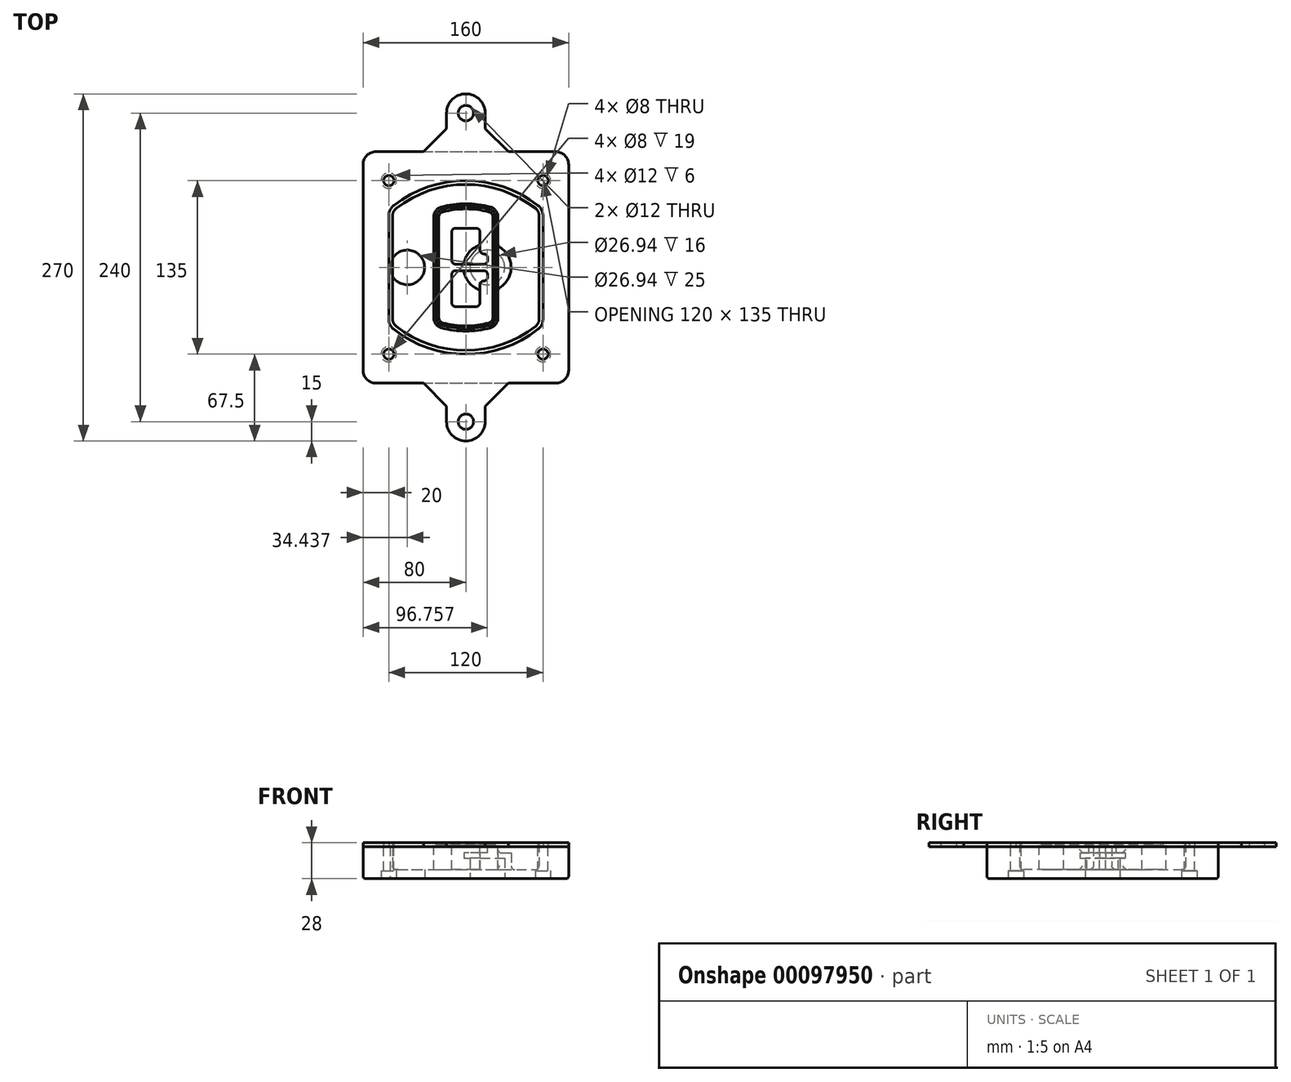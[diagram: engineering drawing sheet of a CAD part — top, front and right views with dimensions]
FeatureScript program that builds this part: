
annotation { "Feature Type Name" : "Feature", "Feature Type Description" : "" }
export const myFeature = defineFeature(function(context is Context, id is Id, definition is map)
    precondition{}
    {
        {
            var Q0;
            Q0=qCreatedBy(makeId("Top.planeOp"),FACE);
            var sketch = newSketch(context, id + "F0", { "sketchPlane" : qUnion([Q0])});
            skPoint(sketch, "E0.rect.middle", {"position": v(0, 0) * mm});
            skLineSegment(sketch, "E1.bottom", {"start": v(-70, -90) * mm, "end": v(70, -90) * mm});
            skLineSegment(sketch, "E1.top", {"start": v(-70, 90) * mm, "end": v(70, 90) * mm});
            skLineSegment(sketch, "E1.left", {"start": v(-80, -80) * mm, "end": v(-80, 80) * mm});
            skLineSegment(sketch, "E1.right", {"start": v(80, -80) * mm, "end": v(80, 80) * mm});
            skLineSegment(sketch, "E2", {"start": v(-80, 90) * mm, "end": v(80, -90) * mm, "construction": true});
            skLineSegment(sketch, "E3", {"start": v(80, 90) * mm, "end": v(-80, -90) * mm, "construction": true});
            skCircle(sketch, "E4", {"center": v(-60, 67.5) * mm, "radius": 4 * mm});
            skCircle(sketch, "E5", {"center": v(60, 67.5) * mm, "radius": 4 * mm});
            skCircle(sketch, "E6", {"center": v(60, -67.5) * mm, "radius": 4 * mm});
            skCircle(sketch, "E7", {"center": v(-60, -67.5) * mm, "radius": 4 * mm});
            skLineSegment(sketch, "E8", {"start": v(-60, 67.5) * mm, "end": v(60, 67.5) * mm, "construction": true});
            skLineSegment(sketch, "E9", {"start": v(60, 67.5) * mm, "end": v(60, -67.5) * mm, "construction": true});
            skLineSegment(sketch, "E10", {"start": v(60, -67.5) * mm, "end": v(-60, -67.5) * mm, "construction": true});
            skLineSegment(sketch, "E11", {"start": v(-60, -67.5) * mm, "end": v(-60, 67.5) * mm, "construction": true});
            skLineSegment(sketch, "E12", {"start": v(-60, 40.3) * mm, "end": v(-60, -40.3) * mm});
            skLineSegment(sketch, "E13", {"start": v(60, 40.3) * mm, "end": v(60, -40.3) * mm});
            skArc(sketch, "E14", {"start": v(56.15, 48.18) * mm, "mid": v(0, 67.5) * mm, "end": v(-56.15, 48.18) * mm});
            skArc(sketch, "E15", {"start": v(-56.15, -48.18) * mm, "mid": v(0, -67.5) * mm, "end": v(56.15, -48.18) * mm});
            skLineSegment(sketch, "E16", {"start": v(-60, 0) * mm, "end": v(60, 0) * mm, "construction": true});
            skPoint(sketch, "E17.visualSharp", {"position": v(-60, -45) * mm});
            skArc(sketch, "E17.filletArc", {"start": v(-60, -40.3) * mm, "mid": v(-58.99, -44.68) * mm, "end": v(-56.15, -48.18) * mm});
            skPoint(sketch, "E18.visualSharp", {"position": v(-60, 45) * mm});
            skArc(sketch, "E18.filletArc", {"start": v(-56.15, 48.18) * mm, "mid": v(-58.99, 44.68) * mm, "end": v(-60, 40.3) * mm});
            skPoint(sketch, "E19.visualSharp", {"position": v(60, 45) * mm});
            skArc(sketch, "E19.filletArc", {"start": v(60, 40.3) * mm, "mid": v(58.99, 44.68) * mm, "end": v(56.15, 48.18) * mm});
            skPoint(sketch, "E20.visualSharp", {"position": v(60, -45) * mm});
            skArc(sketch, "E20.filletArc", {"start": v(56.15, -48.18) * mm, "mid": v(58.99, -44.68) * mm, "end": v(60, -40.3) * mm});
            skPoint(sketch, "E21.visualSharp", {"position": v(-80, 90) * mm});
            skArc(sketch, "E21.filletArc", {"start": v(-70, 90) * mm, "mid": v(-77.07, 87.07) * mm, "end": v(-80, 80) * mm});
            skPoint(sketch, "E22.visualSharp", {"position": v(80, 90) * mm});
            skArc(sketch, "E22.filletArc", {"start": v(80, 80) * mm, "mid": v(77.07, 87.07) * mm, "end": v(70, 90) * mm});
            skPoint(sketch, "E23.visualSharp", {"position": v(80, -90) * mm});
            skArc(sketch, "E23.filletArc", {"start": v(70, -90) * mm, "mid": v(77.07, -87.07) * mm, "end": v(80, -80) * mm});
            skPoint(sketch, "E24.visualSharp", {"position": v(-80, -90) * mm});
            skArc(sketch, "E24.filletArc", {"start": v(-80, -80) * mm, "mid": v(-77.07, -87.07) * mm, "end": v(-70, -90) * mm});
            skArc(sketch, "E25.0", {"start": v(57, 40.3) * mm, "mid": v(56.3, 43.36) * mm, "end": v(54.3, 45.81) * mm});
            skLineSegment(sketch, "E25.1", {"start": v(57, 40.3) * mm, "end": v(57, -40.3) * mm});
            skArc(sketch, "E25.2", {"start": v(54.3, -45.81) * mm, "mid": v(56.3, -43.36) * mm, "end": v(57, -40.3) * mm});
            skArc(sketch, "E25.3", {"start": v(-54.3, -45.81) * mm, "mid": v(0, -64.5) * mm, "end": v(54.3, -45.81) * mm});
            skArc(sketch, "E25.4", {"start": v(-57, -40.3) * mm, "mid": v(-56.3, -43.36) * mm, "end": v(-54.3, -45.81) * mm});
            skArc(sketch, "E25.5", {"start": v(54.3, 45.81) * mm, "mid": v(0, 64.5) * mm, "end": v(-54.3, 45.81) * mm});
            skLineSegment(sketch, "E25.6", {"start": v(-57, 40.3) * mm, "end": v(-57, -40.3) * mm});
            skArc(sketch, "E25.7", {"start": v(-54.3, 45.81) * mm, "mid": v(-56.3, 43.36) * mm, "end": v(-57, 40.3) * mm});
            skArc(sketch, "E26.0", {"start": v(-58.62, 51.33) * mm, "mid": v(-62.58, 46.43) * mm, "end": v(-64, 40.3) * mm});
            skArc(sketch, "E26.1", {"start": v(58.62, 51.33) * mm, "mid": v(0, 71.5) * mm, "end": v(-58.62, 51.33) * mm});
            skArc(sketch, "E26.2", {"start": v(64, 40.3) * mm, "mid": v(62.58, 46.43) * mm, "end": v(58.62, 51.33) * mm});
            skLineSegment(sketch, "E26.3", {"start": v(64, 40.3) * mm, "end": v(64, -40.3) * mm});
            skArc(sketch, "E26.4", {"start": v(58.62, -51.33) * mm, "mid": v(62.58, -46.43) * mm, "end": v(64, -40.3) * mm});
            skLineSegment(sketch, "E26.5", {"start": v(-64, 40.3) * mm, "end": v(-64, -40.3) * mm});
            skArc(sketch, "E26.6", {"start": v(-58.62, -51.33) * mm, "mid": v(0, -71.5) * mm, "end": v(58.62, -51.33) * mm});
            skArc(sketch, "E26.7", {"start": v(-64, -40.3) * mm, "mid": v(-62.58, -46.43) * mm, "end": v(-58.62, -51.33) * mm});
            skSolve(sketch);
        }
        {
            var Q0;
            Q0=makeQuery(id+"F0.imprint","IMPRINT",FACE,{"disambiguationData":[TD([[makeQuery(id+"F0.imprint","IMPRINT",EDGE,{"derivedFrom":sQuery(id+"F0.wireOp",EDGE,"E1.bottom")}),1.0]])]});
            var Q1;
            Q1=makeQuery(id+"F0.imprint","IMPRINT",FACE,{"disambiguationData":[TD([[makeQuery(id+"F0.imprint","IMPRINT",EDGE,{"derivedFrom":sQuery(id+"F0.wireOp",EDGE,"E12")}),1.0]])]});
            var Q2;
            Q2=makeQuery(id+"F0.imprint","IMPRINT",FACE,{"disambiguationData":[TD([[makeQuery(id+"F0.imprint","IMPRINT",EDGE,{"derivedFrom":sQuery(id+"F0.wireOp",EDGE,"E25.0")}),1.0]])]});
            var Q3;
            Q3=makeQuery(id+"F0.imprint","IMPRINT",FACE,{"disambiguationData":[TD([[makeQuery(id+"F0.imprint","IMPRINT",EDGE,{"derivedFrom":sQuery(id+"F0.wireOp",EDGE,"E12")}),-1.0]])]});
            extrude(context, id + "F1", {"entities" : qUnion([Q0, Q1, Q2, Q3]), "oppositeDirection" : true, "depth" : 25 * mm});
        }
        {
            var Q0;
            Q0=makeQuery(id+"F0.imprint","IMPRINT",FACE,{"disambiguationData":[TD([[makeQuery(id+"F0.imprint","IMPRINT",EDGE,{"derivedFrom":sQuery(id+"F0.wireOp",EDGE,"E12")}),1.0]])]});
            extrude(context, id + "F2", {"entities" : qUnion([Q0]), "operationType" : NewBodyOperationType.ADD, "depth" : 3 * mm});
        }
        {
            var Q0;
            Q0=makeQuery(id+"F0.imprint","IMPRINT",FACE,{"disambiguationData":[TD([[makeQuery(id+"F0.imprint","IMPRINT",EDGE,{"derivedFrom":sQuery(id+"F0.wireOp",EDGE,"E25.0")}),1.0]])]});
            extrude(context, id + "F3", {"entities" : qUnion([Q0]), "operationType" : NewBodyOperationType.REMOVE, "oppositeDirection" : true, "depth" : 18 * mm});
        }
        {
            var Q0;
            Q0=makeQuery(id+"F2.opExtrude","CAP_FACE",FACE,{"disambiguationData":[OSD([sQuery(id+"F0.wireOp",EDGE,"E12"),sQuery(id+"F0.wireOp",EDGE,"E13"),sQuery(id+"F0.wireOp",EDGE,"E14"),sQuery(id+"F0.wireOp",EDGE,"E15"),sQuery(id+"F0.wireOp",EDGE,"E17.filletArc"),sQuery(id+"F0.wireOp",EDGE,"E18.filletArc"),sQuery(id+"F0.wireOp",EDGE,"E19.filletArc"),sQuery(id+"F0.wireOp",EDGE,"E20.filletArc"),sQuery(id+"F0.wireOp",EDGE,"E25.0"),sQuery(id+"F0.wireOp",EDGE,"E25.1"),sQuery(id+"F0.wireOp",EDGE,"E25.2"),sQuery(id+"F0.wireOp",EDGE,"E25.3"),sQuery(id+"F0.wireOp",EDGE,"E25.4"),sQuery(id+"F0.wireOp",EDGE,"E25.5"),sQuery(id+"F0.wireOp",EDGE,"E25.6"),sQuery(id+"F0.wireOp",EDGE,"E25.7")])],"isStart":false});
            var sketch = newSketch(context, id + "F4", { "sketchPlane" : qUnion([Q0])});
            skArc(sketch, "E27.0", {"start": v(-19.08, -46.97) * mm, "mid": v(0, -49.5) * mm, "end": v(19.08, -46.97) * mm});
            skArc(sketch, "E28.0", {"start": v(19.08, 46.97) * mm, "mid": v(0, 49.5) * mm, "end": v(-19.08, 46.97) * mm});
            skLineSegment(sketch, "E29", {"start": v(-25, 39.25) * mm, "end": v(-25, -39.25) * mm});
            skLineSegment(sketch, "E30", {"start": v(25, 39.25) * mm, "end": v(25, -39.25) * mm});
            skLineSegment(sketch, "E31", {"start": v(-25, 45.1) * mm, "end": v(25, 45.1) * mm, "construction": true});
            skLineSegment(sketch, "E32", {"start": v(-25, -45.1) * mm, "end": v(25, -45.1) * mm, "construction": true});
            skPoint(sketch, "E33.visualSharp", {"position": v(-25, 45.1) * mm});
            skArc(sketch, "E33.filletArc", {"start": v(-19.08, 46.97) * mm, "mid": v(-23.35, 44.11) * mm, "end": v(-25, 39.25) * mm});
            skPoint(sketch, "E34.visualSharp", {"position": v(25, 45.1) * mm});
            skArc(sketch, "E34.filletArc", {"start": v(25, 39.25) * mm, "mid": v(23.35, 44.11) * mm, "end": v(19.08, 46.97) * mm});
            skPoint(sketch, "E35.visualSharp", {"position": v(25, -45.1) * mm});
            skArc(sketch, "E35.filletArc", {"start": v(19.08, -46.97) * mm, "mid": v(23.35, -44.11) * mm, "end": v(25, -39.25) * mm});
            skPoint(sketch, "E36.visualSharp", {"position": v(-25, -45.1) * mm});
            skArc(sketch, "E36.filletArc", {"start": v(-25, -39.25) * mm, "mid": v(-23.35, -44.11) * mm, "end": v(-19.08, -46.97) * mm});
            skArc(sketch, "E37.0", {"start": v(54.3, 45.81) * mm, "mid": v(0, 64.5) * mm, "end": v(-54.3, 45.81) * mm});
            skArc(sketch, "E37.1", {"start": v(-54.3, 45.81) * mm, "mid": v(-56.3, 43.36) * mm, "end": v(-57, 40.3) * mm});
            skLineSegment(sketch, "E37.2", {"start": v(-57, 40.3) * mm, "end": v(-57, -40.3) * mm});
            skArc(sketch, "E37.3", {"start": v(-57, -40.3) * mm, "mid": v(-56.3, -43.36) * mm, "end": v(-54.3, -45.81) * mm});
            skArc(sketch, "E37.4", {"start": v(-54.3, -45.81) * mm, "mid": v(0, -64.5) * mm, "end": v(54.3, -45.81) * mm});
            skArc(sketch, "E37.5", {"start": v(54.3, -45.81) * mm, "mid": v(56.3, -43.36) * mm, "end": v(57, -40.3) * mm});
            skLineSegment(sketch, "E37.6", {"start": v(57, 40.3) * mm, "end": v(57, -40.3) * mm});
            skArc(sketch, "E37.7", {"start": v(57, 40.3) * mm, "mid": v(56.3, 43.36) * mm, "end": v(54.3, 45.81) * mm});
            skLineSegment(sketch, "E38.0", {"start": v(23, 39.25) * mm, "end": v(23, -39.25) * mm});
            skArc(sketch, "E38.1", {"start": v(18.56, -45.04) * mm, "mid": v(21.76, -42.9) * mm, "end": v(23, -39.25) * mm});
            skArc(sketch, "E38.2", {"start": v(-18.56, -45.04) * mm, "mid": v(0, -47.5) * mm, "end": v(18.56, -45.04) * mm});
            skArc(sketch, "E38.3", {"start": v(-23, -39.25) * mm, "mid": v(-21.76, -42.9) * mm, "end": v(-18.56, -45.04) * mm});
            skLineSegment(sketch, "E38.4", {"start": v(-23, 39.25) * mm, "end": v(-23, -39.25) * mm});
            skArc(sketch, "E38.5", {"start": v(23, 39.25) * mm, "mid": v(21.76, 42.9) * mm, "end": v(18.56, 45.04) * mm});
            skArc(sketch, "E38.6", {"start": v(-18.56, 45.04) * mm, "mid": v(-21.76, 42.9) * mm, "end": v(-23, 39.25) * mm});
            skArc(sketch, "E38.7", {"start": v(18.56, 45.04) * mm, "mid": v(0, 47.5) * mm, "end": v(-18.56, 45.04) * mm});
            skArc(sketch, "E39.0", {"start": v(21, 39.25) * mm, "mid": v(20.18, 41.68) * mm, "end": v(18.04, 43.1) * mm});
            skLineSegment(sketch, "E39.1", {"start": v(21, 39.25) * mm, "end": v(21, -39.25) * mm});
            skArc(sketch, "E39.2", {"start": v(18.04, -43.1) * mm, "mid": v(20.18, -41.68) * mm, "end": v(21, -39.25) * mm});
            skArc(sketch, "E39.3", {"start": v(-18.04, -43.1) * mm, "mid": v(0, -45.5) * mm, "end": v(18.04, -43.1) * mm});
            skArc(sketch, "E39.4", {"start": v(-21, -39.25) * mm, "mid": v(-20.18, -41.68) * mm, "end": v(-18.04, -43.1) * mm});
            skArc(sketch, "E39.5", {"start": v(18.04, 43.1) * mm, "mid": v(0, 45.5) * mm, "end": v(-18.04, 43.1) * mm});
            skLineSegment(sketch, "E39.6", {"start": v(-21, 39.25) * mm, "end": v(-21, -39.25) * mm});
            skArc(sketch, "E39.7", {"start": v(-18.04, 43.1) * mm, "mid": v(-20.18, 41.68) * mm, "end": v(-21, 39.25) * mm});
            skLineSegment(sketch, "E40", {"start": v(-25, 0) * mm, "end": v(25, 0) * mm, "construction": true});
            skLineSegment(sketch, "E41", {"start": v(-11, 5.5) * mm, "end": v(-11, 27.5) * mm});
            skLineSegment(sketch, "E42", {"start": v(-8, 30.5) * mm, "end": v(8, 30.5) * mm});
            skLineSegment(sketch, "E43", {"start": v(11, 27.5) * mm, "end": v(11, 13.5) * mm});
            skLineSegment(sketch, "E44", {"start": v(14, 10.5) * mm, "end": v(14, 10.5) * mm});
            skLineSegment(sketch, "E45", {"start": v(17, 7.5) * mm, "end": v(17, 5.5) * mm});
            skLineSegment(sketch, "E46", {"start": v(14, 2.5) * mm, "end": v(-8, 2.5) * mm});
            skPoint(sketch, "E47.visualSharp", {"position": v(-11, 30.5) * mm});
            skArc(sketch, "E47.filletArc", {"start": v(-8, 30.5) * mm, "mid": v(-10.12, 29.62) * mm, "end": v(-11, 27.5) * mm});
            skPoint(sketch, "E48.visualSharp", {"position": v(11, 30.5) * mm});
            skArc(sketch, "E48.filletArc", {"start": v(11, 27.5) * mm, "mid": v(10.12, 29.62) * mm, "end": v(8, 30.5) * mm});
            skPoint(sketch, "E49.visualSharp", {"position": v(11, 10.5) * mm});
            skArc(sketch, "E49.filletArc", {"start": v(11, 13.5) * mm, "mid": v(11.88, 11.38) * mm, "end": v(14, 10.5) * mm});
            skPoint(sketch, "E50.visualSharp", {"position": v(17, 10.5) * mm});
            skArc(sketch, "E50.filletArc", {"start": v(17, 7.5) * mm, "mid": v(16.12, 9.62) * mm, "end": v(14, 10.5) * mm});
            skPoint(sketch, "E51.visualSharp", {"position": v(17, 2.5) * mm});
            skArc(sketch, "E51.filletArc", {"start": v(14, 2.5) * mm, "mid": v(16.12, 3.38) * mm, "end": v(17, 5.5) * mm});
            skPoint(sketch, "E52.visualSharp", {"position": v(-11, 2.5) * mm});
            skArc(sketch, "E52.filletArc", {"start": v(-11, 5.5) * mm, "mid": v(-10.12, 3.38) * mm, "end": v(-8, 2.5) * mm});
            skLineSegment(sketch, "E53.0.MirrorCS", {"start": v(14, -2.5) * mm, "end": v(-8, -2.5) * mm});
            skArc(sketch, "E54.0.MirrorCS", {"start": v(-11, -5.5) * mm, "mid": v(-10.12, -3.38) * mm, "end": v(-8, -2.5) * mm});
            skLineSegment(sketch, "E55.0.MirrorCS", {"start": v(-11, -5.5) * mm, "end": v(-11, -27.5) * mm});
            skArc(sketch, "E56.0.MirrorCS", {"start": v(-8, -30.5) * mm, "mid": v(-10.12, -29.62) * mm, "end": v(-11, -27.5) * mm});
            skLineSegment(sketch, "E57.0.MirrorCS", {"start": v(-8, -30.5) * mm, "end": v(8, -30.5) * mm});
            skArc(sketch, "E58.0.MirrorCS", {"start": v(11, -27.5) * mm, "mid": v(10.12, -29.62) * mm, "end": v(8, -30.5) * mm});
            skLineSegment(sketch, "E59.0.MirrorCS", {"start": v(11, -27.5) * mm, "end": v(11, -13.5) * mm});
            skArc(sketch, "E60.0.MirrorCS", {"start": v(11, -13.5) * mm, "mid": v(11.88, -11.38) * mm, "end": v(14, -10.5) * mm});
            skArc(sketch, "E61.0.MirrorCS", {"start": v(17, -7.5) * mm, "mid": v(16.12, -9.62) * mm, "end": v(14, -10.5) * mm});
            skLineSegment(sketch, "E62.0.MirrorCS", {"start": v(17, -7.5) * mm, "end": v(17, -5.5) * mm});
            skArc(sketch, "E63.0.MirrorCS", {"start": v(14, -2.5) * mm, "mid": v(16.12, -3.38) * mm, "end": v(17, -5.5) * mm});
            skSolve(sketch);
        }
        {
            var Q0;
            Q0=makeQuery(id+"F4.imprint","IMPRINT",FACE,{"disambiguationData":[TD([[makeQuery(id+"F4.imprint","IMPRINT",EDGE,{"derivedFrom":sQuery(id+"F4.wireOp",EDGE,"E27.0")}),1.0]])]});
            var Q1;
            Q1=makeQuery(id+"F4.imprint","IMPRINT",FACE,{"disambiguationData":[TD([[makeQuery(id+"F4.imprint","IMPRINT",EDGE,{"derivedFrom":sQuery(id+"F4.wireOp",EDGE,"E38.0")}),-1.0]])]});
            var Q2;
            Q2=makeQuery(id+"F4.imprint","IMPRINT",FACE,{"disambiguationData":[TD([[makeQuery(id+"F4.imprint","IMPRINT",EDGE,{"derivedFrom":sQuery(id+"F4.wireOp",EDGE,"E39.0")}),1.0]])]});
            extrude(context, id + "F5", {"entities" : qUnion([Q0, Q1, Q2]), "operationType" : NewBodyOperationType.ADD, "endBound" : BoundingType.UP_TO_NEXT, "oppositeDirection" : true, "depth" : 25 * mm});
        }
        {
            var Q0;
            Q0=makeQuery(id+"F4.imprint","IMPRINT",FACE,{"disambiguationData":[TD([[makeQuery(id+"F4.imprint","IMPRINT",EDGE,{"derivedFrom":sQuery(id+"F4.wireOp",EDGE,"E38.0")}),-1.0]])]});
            extrude(context, id + "F6", {"entities" : qUnion([Q0]), "operationType" : NewBodyOperationType.REMOVE, "oppositeDirection" : true, "depth" : 2 * mm});
        }
        {
            var Q0;
            Q0=makeQuery(id+"F1.opExtrude","CAP_FACE",FACE,{"disambiguationData":[OSD([sQuery(id+"F0.wireOp",EDGE,"E1.bottom"),sQuery(id+"F0.wireOp",EDGE,"E1.top"),sQuery(id+"F0.wireOp",EDGE,"E1.left"),sQuery(id+"F0.wireOp",EDGE,"E1.right"),sQuery(id+"F0.wireOp",EDGE,"E4"),sQuery(id+"F0.wireOp",EDGE,"E5"),sQuery(id+"F0.wireOp",EDGE,"E6"),sQuery(id+"F0.wireOp",EDGE,"E7"),sQuery(id+"F0.wireOp",EDGE,"E21.filletArc"),sQuery(id+"F0.wireOp",EDGE,"E22.filletArc"),sQuery(id+"F0.wireOp",EDGE,"E23.filletArc"),sQuery(id+"F0.wireOp",EDGE,"E24.filletArc")])],"isStart":false});
            var sketch = newSketch(context, id + "F7", { "sketchPlane" : qUnion([Q0])});
            skCircle(sketch, "E64", {"center": v(16.76, 0) * mm, "radius": 13.47 * mm});
            skCircle(sketch, "E65", {"center": v(-45.56, 0) * mm, "radius": 13.47 * mm});
            skLineSegment(sketch, "E66", {"start": v(80, 0) * mm, "end": v(-80, 0) * mm});
            skCircle(sketch, "E67", {"center": v(16.76, 0) * mm, "radius": 18.47 * mm});
            skCircle(sketch, "E68", {"center": v(60, -67.5) * mm, "radius": 6 * mm});
            skCircle(sketch, "E69", {"center": v(-60, -67.5) * mm, "radius": 6 * mm});
            skCircle(sketch, "E70", {"center": v(-60, 67.5) * mm, "radius": 6 * mm});
            skCircle(sketch, "E71", {"center": v(60, 67.5) * mm, "radius": 6 * mm});
            skSolve(sketch);
        }
        {
            var Q0;
            {var subQ1=sQuery(id+"F7.wireOp",EDGE,"E66");var subQ4=sQuery(id+"F7.wireOp",EDGE,"E64");var subQ6=makeQuery(id+"F7.imprint","INTERSECT",VERTEX,{"disambiguationData":[OD(0.0)],"derivedFrom":[subQ4,subQ1]});Q0=makeQuery(id+"F7.imprint","IMPRINT",FACE,{"disambiguationData":[TD([[makeQuery(id+"F7.imprint","IMPRINT",EDGE,{"disambiguationData":[TD([[subQ6,-1.0]])],"derivedFrom":subQ4}),-1.0]])]});}
            var Q1;
            {var subQ0=sQuery(id+"F7.wireOp",EDGE,"E66");var subQ1=sQuery(id+"F7.wireOp",EDGE,"E64");var subQ3=makeQuery(id+"F7.imprint","INTERSECT",VERTEX,{"disambiguationData":[OD(0.0)],"derivedFrom":[subQ1,subQ0]});Q1=makeQuery(id+"F7.imprint","IMPRINT",FACE,{"disambiguationData":[TD([[makeQuery(id+"F7.imprint","IMPRINT",EDGE,{"disambiguationData":[TD([[subQ3,-1.0]])],"derivedFrom":subQ1}),1.0]])]});}
            var Q2;
            {var subQ0=sQuery(id+"F7.wireOp",EDGE,"E66");var subQ1=sQuery(id+"F7.wireOp",EDGE,"E64");var subQ3=makeQuery(id+"F7.imprint","INTERSECT",VERTEX,{"disambiguationData":[OD(0.0)],"derivedFrom":[subQ1,subQ0]});Q2=makeQuery(id+"F7.imprint","IMPRINT",FACE,{"disambiguationData":[TD([[makeQuery(id+"F7.imprint","IMPRINT",EDGE,{"disambiguationData":[TD([[subQ3,1.0]])],"derivedFrom":subQ1}),1.0]])]});}
            var Q3;
            {var subQ1=sQuery(id+"F7.wireOp",EDGE,"E66");var subQ4=sQuery(id+"F7.wireOp",EDGE,"E64");var subQ6=makeQuery(id+"F7.imprint","INTERSECT",VERTEX,{"disambiguationData":[OD(0.0)],"derivedFrom":[subQ4,subQ1]});Q3=makeQuery(id+"F7.imprint","IMPRINT",FACE,{"disambiguationData":[TD([[makeQuery(id+"F7.imprint","IMPRINT",EDGE,{"disambiguationData":[TD([[subQ6,1.0]])],"derivedFrom":subQ4}),-1.0]])]});}
            extrude(context, id + "F8", {"entities" : qUnion([Q0, Q1, Q2, Q3]), "operationType" : NewBodyOperationType.ADD, "oppositeDirection" : true, "depth" : 20 * mm});
        }
        {
            var Q0;
            {var subQ0=sQuery(id+"F7.wireOp",EDGE,"E66");var subQ1=sQuery(id+"F7.wireOp",EDGE,"E64");var subQ3=makeQuery(id+"F7.imprint","INTERSECT",VERTEX,{"disambiguationData":[OD(0.0)],"derivedFrom":[subQ1,subQ0]});Q0=makeQuery(id+"F7.imprint","IMPRINT",FACE,{"disambiguationData":[TD([[makeQuery(id+"F7.imprint","IMPRINT",EDGE,{"disambiguationData":[TD([[subQ3,-1.0]])],"derivedFrom":subQ1}),1.0]])]});}
            var Q1;
            {var subQ0=sQuery(id+"F7.wireOp",EDGE,"E66");var subQ1=sQuery(id+"F7.wireOp",EDGE,"E64");var subQ3=makeQuery(id+"F7.imprint","INTERSECT",VERTEX,{"disambiguationData":[OD(0.0)],"derivedFrom":[subQ1,subQ0]});Q1=makeQuery(id+"F7.imprint","IMPRINT",FACE,{"disambiguationData":[TD([[makeQuery(id+"F7.imprint","IMPRINT",EDGE,{"disambiguationData":[TD([[subQ3,1.0]])],"derivedFrom":subQ1}),1.0]])]});}
            extrude(context, id + "F9", {"entities" : qUnion([Q0, Q1]), "operationType" : NewBodyOperationType.REMOVE, "oppositeDirection" : true, "depth" : 16 * mm});
        }
        {
            var Q0;
            {var subQ0=sQuery(id+"F7.wireOp",EDGE,"E66");var subQ1=sQuery(id+"F7.wireOp",EDGE,"E65");var subQ3=makeQuery(id+"F7.imprint","INTERSECT",VERTEX,{"disambiguationData":[OD(0.0)],"derivedFrom":[subQ1,subQ0]});Q0=makeQuery(id+"F7.imprint","IMPRINT",FACE,{"disambiguationData":[TD([[makeQuery(id+"F7.imprint","IMPRINT",EDGE,{"disambiguationData":[TD([[subQ3,-1.0]])],"derivedFrom":subQ1}),1.0]])]});}
            var Q1;
            {var subQ0=sQuery(id+"F7.wireOp",EDGE,"E66");var subQ1=sQuery(id+"F7.wireOp",EDGE,"E65");var subQ3=makeQuery(id+"F7.imprint","INTERSECT",VERTEX,{"disambiguationData":[OD(0.0)],"derivedFrom":[subQ1,subQ0]});Q1=makeQuery(id+"F7.imprint","IMPRINT",FACE,{"disambiguationData":[TD([[makeQuery(id+"F7.imprint","IMPRINT",EDGE,{"disambiguationData":[TD([[subQ3,1.0]])],"derivedFrom":subQ1}),1.0]])]});}
            extrude(context, id + "F10", {"entities" : qUnion([Q0, Q1]), "operationType" : NewBodyOperationType.REMOVE, "oppositeDirection" : true, "depth" : 25 * mm});
        }
        {
            var Q0;
            Q0=makeQuery(id+"F7.imprint","IMPRINT",FACE,{"disambiguationData":[TD([[makeQuery(id+"F7.imprint","IMPRINT",EDGE,{"derivedFrom":sQuery(id+"F7.wireOp",EDGE,"E68")}),1.0]])]});
            var Q1;
            Q1=makeQuery(id+"F7.imprint","IMPRINT",FACE,{"disambiguationData":[TD([[makeQuery(id+"F7.imprint","IMPRINT",EDGE,{"derivedFrom":makeQuery(id+"F1.opExtrude","CAP_EDGE",EDGE,{"disambiguationData":[OSD([sQuery(id+"F0.wireOp",EDGE,"E5")])],"isStart":false})}),-1.0]])]});
            var Q2;
            Q2=makeQuery(id+"F7.imprint","IMPRINT",FACE,{"disambiguationData":[TD([[makeQuery(id+"F7.imprint","IMPRINT",EDGE,{"derivedFrom":sQuery(id+"F7.wireOp",EDGE,"E69")}),1.0]])]});
            var Q3;
            Q3=makeQuery(id+"F7.imprint","IMPRINT",FACE,{"disambiguationData":[TD([[makeQuery(id+"F7.imprint","IMPRINT",EDGE,{"derivedFrom":makeQuery(id+"F1.opExtrude","CAP_EDGE",EDGE,{"disambiguationData":[OSD([sQuery(id+"F0.wireOp",EDGE,"E4")])],"isStart":false})}),-1.0]])]});
            var Q4;
            Q4=makeQuery(id+"F7.imprint","IMPRINT",FACE,{"disambiguationData":[TD([[makeQuery(id+"F7.imprint","IMPRINT",EDGE,{"derivedFrom":sQuery(id+"F7.wireOp",EDGE,"E70")}),1.0]])]});
            var Q5;
            Q5=makeQuery(id+"F7.imprint","IMPRINT",FACE,{"disambiguationData":[TD([[makeQuery(id+"F7.imprint","IMPRINT",EDGE,{"derivedFrom":makeQuery(id+"F1.opExtrude","CAP_EDGE",EDGE,{"disambiguationData":[OSD([sQuery(id+"F0.wireOp",EDGE,"E7")])],"isStart":false})}),-1.0]])]});
            var Q6;
            Q6=makeQuery(id+"F7.imprint","IMPRINT",FACE,{"disambiguationData":[TD([[makeQuery(id+"F7.imprint","IMPRINT",EDGE,{"derivedFrom":sQuery(id+"F7.wireOp",EDGE,"E71")}),1.0]])]});
            var Q7;
            Q7=makeQuery(id+"F7.imprint","IMPRINT",FACE,{"disambiguationData":[TD([[makeQuery(id+"F7.imprint","IMPRINT",EDGE,{"derivedFrom":makeQuery(id+"F1.opExtrude","CAP_EDGE",EDGE,{"disambiguationData":[OSD([sQuery(id+"F0.wireOp",EDGE,"E6")])],"isStart":false})}),-1.0]])]});
            extrude(context, id + "F11", {"entities" : qUnion([Q0, Q1, Q2, Q3, Q4, Q5, Q6, Q7]), "operationType" : NewBodyOperationType.REMOVE, "oppositeDirection" : true, "depth" : 6 * mm});
        }
        {
            var Q0;
            Q0=makeQuery(id+"F9.boolean.opBoolean","COPY",FACE,{"derivedFrom":makeQuery(id+"F9.opExtrude","CAP_FACE",FACE,{"disambiguationData":[OSD([sQuery(id+"F7.wireOp",EDGE,"E64")])],"isStart":false})});
            var sketch = newSketch(context, id + "F12", { "sketchPlane" : qUnion([Q0])});
            skArc(sketch, "E72.0", {"start": v(11, 17.55) * mm, "mid": v(2.57, 11.82) * mm, "end": v(-1.54, 2.5) * mm});
            skArc(sketch, "E72.1", {"start": v(-1.54, -2.5) * mm, "mid": v(2.57, -11.82) * mm, "end": v(11, -17.55) * mm});
            skLineSegment(sketch, "E73", {"start": v(-1.54, -2.5) * mm, "end": v(14, -2.5) * mm});
            skLineSegment(sketch, "E74.0", {"start": v(14, 2.5) * mm, "end": v(-1.54, 2.5) * mm});
            skArc(sketch, "E74.1", {"start": v(14, 2.5) * mm, "mid": v(16.12, 3.38) * mm, "end": v(17, 5.5) * mm});
            skLineSegment(sketch, "E74.2", {"start": v(17, 7.5) * mm, "end": v(17, 5.5) * mm});
            skArc(sketch, "E74.3", {"start": v(17, 7.5) * mm, "mid": v(16.12, 9.62) * mm, "end": v(14, 10.5) * mm});
            skArc(sketch, "E74.4", {"start": v(11, 13.5) * mm, "mid": v(11.88, 11.38) * mm, "end": v(14, 10.5) * mm});
            skLineSegment(sketch, "E74.5", {"start": v(11, 17.55) * mm, "end": v(11, 13.5) * mm});
            skLineSegment(sketch, "E74.7", {"start": v(14, -2.5) * mm, "end": v(-1.54, -2.5) * mm});
            skArc(sketch, "E74.8", {"start": v(14, -2.5) * mm, "mid": v(16.12, -3.38) * mm, "end": v(17, -5.5) * mm});
            skLineSegment(sketch, "E74.9", {"start": v(17, -7.5) * mm, "end": v(17, -5.5) * mm});
            skArc(sketch, "E74.10", {"start": v(17, -7.5) * mm, "mid": v(16.12, -9.62) * mm, "end": v(14, -10.5) * mm});
            skArc(sketch, "E74.11", {"start": v(11, -13.5) * mm, "mid": v(11.88, -11.38) * mm, "end": v(14, -10.5) * mm});
            skLineSegment(sketch, "E74.12", {"start": v(11, -17.55) * mm, "end": v(11, -13.5) * mm});
            skPoint(sketch, "E75.orphan", {"position": v(11, -27.5) * mm});
            skPoint(sketch, "E76.orphan", {"position": v(-8, -2.5) * mm});
            skPoint(sketch, "E77.orphan", {"position": v(-8, 2.5) * mm});
            skPoint(sketch, "E78.orphan", {"position": v(11, 27.5) * mm});
            skSolve(sketch);
        }
        {
            var Q0;
            {var subQ7=sQuery(id+"F12.wireOp",EDGE,"E72.0");var subQ14=sQuery(id+"F12.wireOp",EDGE,"E72.1");var subQ16=sQuery(id+"F12.wireOp",EDGE,"E74.1");var subQ18=sQuery(id+"F12.wireOp",EDGE,"E74.8");Q0=qUnion([makeQuery(id+"F12.imprint","IMPRINT",FACE,{"disambiguationData":[TD([[makeQuery(id+"F12.imprint","IMPRINT",EDGE,{"derivedFrom":subQ7}),1.0]])]}),makeQuery(id+"F12.imprint","IMPRINT",FACE,{"disambiguationData":[TD([[makeQuery(id+"F12.imprint","IMPRINT",EDGE,{"derivedFrom":subQ14}),1.0]])]}),makeQuery(id+"F12.imprint","IMPRINT",FACE,{"disambiguationData":[TD([[makeQuery(id+"F12.imprint","IMPRINT",EDGE,{"derivedFrom":subQ16}),1.0]])]}),makeQuery(id+"F12.imprint","IMPRINT",FACE,{"disambiguationData":[TD([[makeQuery(id+"F12.imprint","IMPRINT",EDGE,{"derivedFrom":subQ18}),-1.0]])]})]);}
            var Q1;
            Q1=makeQuery(id+"F5.boolean.opBoolean","SPLIT",FACE,{"disambiguationData":[TD([makeQuery(id+"F5.opExtrude","SWEPT_FACE",FACE,{"disambiguationData":[OSD([sQuery(id+"F4.wireOp",EDGE,"E41")])]})])],"derivedFrom":makeQuery(id+"F3.boolean.opBoolean","COPY",FACE,{"derivedFrom":makeQuery(id+"F3.opExtrude","CAP_FACE",FACE,{"disambiguationData":[OSD([sQuery(id+"F0.wireOp",EDGE,"E25.0"),sQuery(id+"F0.wireOp",EDGE,"E25.1"),sQuery(id+"F0.wireOp",EDGE,"E25.2"),sQuery(id+"F0.wireOp",EDGE,"E25.3"),sQuery(id+"F0.wireOp",EDGE,"E25.4"),sQuery(id+"F0.wireOp",EDGE,"E25.5"),sQuery(id+"F0.wireOp",EDGE,"E25.6"),sQuery(id+"F0.wireOp",EDGE,"E25.7")])],"isStart":false})})});
            extrude(context, id + "F13", {"entities" : qUnion([Q0]), "operationType" : NewBodyOperationType.REMOVE, "endBound" : BoundingType.UP_TO_SURFACE, "endBoundEntityFace" : qUnion([Q1]), "depth" : 25 * mm});
        }
        {
            var Q0;
            Q0=makeQuery(id+"F3.boolean.opBoolean","COPY",EDGE,{"derivedFrom":makeQuery(id+"F3.opExtrude","CAP_EDGE",EDGE,{"disambiguationData":[OSD([sQuery(id+"F0.wireOp",EDGE,"E25.6")])],"isStart":false})});
            var Q1;
            Q1=makeQuery(id+"F8.boolean.opBoolean","INTERSECT",EDGE,{"derivedFrom":[makeQuery(id+"F5.opExtrude","SWEPT_FACE",FACE,{"disambiguationData":[OSD([sQuery(id+"F4.wireOp",EDGE,"E30")])]}),makeQuery(id+"F8.opExtrude","CAP_FACE",FACE,{"disambiguationData":[OSD([sQuery(id+"F7.wireOp",EDGE,"E67")])],"isStart":false})]});
            var Q2;
            Q2=makeQuery(id+"F8.boolean.opBoolean","INTERSECT",EDGE,{"disambiguationData":[OD(1.0)],"derivedFrom":[makeQuery(id+"F5.opExtrude","SWEPT_FACE",FACE,{"disambiguationData":[OSD([sQuery(id+"F4.wireOp",EDGE,"E30")])]}),makeQuery(id+"F8.opExtrude","SWEPT_FACE",FACE,{"disambiguationData":[OSD([sQuery(id+"F7.wireOp",EDGE,"E67")])]})]});
            var Q3;
            {var subQ0=sQuery(id+"F4.wireOp",EDGE,"E30");Q3=makeQuery(id+"F8.boolean.opBoolean","SPLIT",EDGE,{"disambiguationData":[TD([makeQuery(id+"F5.opExtrude","SWEPT_FACE",FACE,{"disambiguationData":[OSD([sQuery(id+"F4.wireOp",EDGE,"E35.filletArc")])]})])],"derivedFrom":makeQuery(id+"F5.opExtrude","CAP_EDGE",EDGE,{"disambiguationData":[OSD([subQ0])],"isStart":false})});}
            var Q4;
            {var subQ0=sQuery(id+"F0.wireOp",EDGE,"E25.7");var subQ1=sQuery(id+"F0.wireOp",EDGE,"E25.1");var subQ2=sQuery(id+"F0.wireOp",EDGE,"E25.6");var subQ3=sQuery(id+"F0.wireOp",EDGE,"E25.5");var subQ4=sQuery(id+"F0.wireOp",EDGE,"E25.4");var subQ5=sQuery(id+"F0.wireOp",EDGE,"E25.0");var subQ6=sQuery(id+"F0.wireOp",EDGE,"E25.2");var subQ7=sQuery(id+"F0.wireOp",EDGE,"E25.3");Q4=makeQuery(id+"F8.boolean.opBoolean","INTERSECT",EDGE,{"derivedFrom":[makeQuery(id+"F5.boolean.opBoolean","SPLIT",FACE,{"disambiguationData":[TD([makeQuery(id+"F2.opExtrude","SWEPT_FACE",FACE,{"disambiguationData":[OSD([subQ5])]})])],"derivedFrom":makeQuery(id+"F3.boolean.opBoolean","COPY",FACE,{"derivedFrom":makeQuery(id+"F3.opExtrude","CAP_FACE",FACE,{"disambiguationData":[OSD([subQ5,subQ1,subQ6,subQ7,subQ4,subQ3,subQ2,subQ0])],"isStart":false})})}),makeQuery(id+"F8.opExtrude","SWEPT_FACE",FACE,{"disambiguationData":[OSD([sQuery(id+"F7.wireOp",EDGE,"E67")])]})]});}
            var Q5;
            Q5=makeQuery(id+"F8.boolean.opBoolean","INTERSECT",EDGE,{"disambiguationData":[OD(0.0)],"derivedFrom":[makeQuery(id+"F5.opExtrude","SWEPT_FACE",FACE,{"disambiguationData":[OSD([sQuery(id+"F4.wireOp",EDGE,"E30")])]}),makeQuery(id+"F8.opExtrude","SWEPT_FACE",FACE,{"disambiguationData":[OSD([sQuery(id+"F7.wireOp",EDGE,"E67")])]})]});
            fillet(context, id + "F14", {"entities" : qUnion([Q0, Q1, Q2, Q3, Q4, Q5]), "radius" : 3 * mm, "tangentPropagation" : true, "allowEdgeOverflow" : false});
        }
        {
            var Q0;
            Q0=makeQuery(id+"F1.opExtrude","CAP_EDGE",EDGE,{"disambiguationData":[OSD([sQuery(id+"F0.wireOp",EDGE,"E1.bottom")])],"isStart":false});
            fillet(context, id + "F15", {"entities" : qUnion([Q0]), "radius" : 2 * mm, "tangentPropagation" : true, "allowEdgeOverflow" : false});
        }
        {
            var Q0;
            {var subQ0=sQuery(id+"F0.wireOp",EDGE,"E22.filletArc");var subQ1=sQuery(id+"F0.wireOp",EDGE,"E7");var subQ2=sQuery(id+"F0.wireOp",EDGE,"E6");var subQ3=sQuery(id+"F0.wireOp",EDGE,"E5");var subQ4=sQuery(id+"F0.wireOp",EDGE,"E4");var subQ5=sQuery(id+"F0.wireOp",EDGE,"E1.bottom");var subQ6=sQuery(id+"F0.wireOp",EDGE,"E21.filletArc");var subQ7=sQuery(id+"F0.wireOp",EDGE,"E1.top");var subQ8=sQuery(id+"F0.wireOp",EDGE,"E1.left");var subQ9=sQuery(id+"F0.wireOp",EDGE,"E1.right");var subQ10=sQuery(id+"F0.wireOp",EDGE,"E23.filletArc");var subQ11=sQuery(id+"F0.wireOp",EDGE,"E24.filletArc");Q0=makeQuery(id+"F2.boolean.opBoolean","SPLIT",FACE,{"disambiguationData":[TD([makeQuery(id+"F1.opExtrude","SWEPT_FACE",FACE,{"disambiguationData":[OSD([subQ5])]})])],"derivedFrom":makeQuery(id+"F1.opExtrude","CAP_FACE",FACE,{"disambiguationData":[OSD([subQ5,subQ7,subQ8,subQ9,subQ4,subQ3,subQ2,subQ1,subQ6,subQ0,subQ10,subQ11])],"isStart":true})});}
            var sketch = newSketch(context, id + "F16", { "sketchPlane" : qUnion([Q0])});
            skLineSegment(sketch, "E79.0", {"start": v(-70, 90) * mm, "end": v(70, 90) * mm});
            skArc(sketch, "E79.1", {"start": v(-70, 90) * mm, "mid": v(-77.07, 87.07) * mm, "end": v(-80, 80) * mm});
            skArc(sketch, "E79.2", {"start": v(80, 80) * mm, "mid": v(77.07, 87.07) * mm, "end": v(70, 90) * mm});
            skLineSegment(sketch, "E79.3", {"start": v(80, -80) * mm, "end": v(80, 80) * mm});
            skLineSegment(sketch, "E79.4", {"start": v(-80, -80) * mm, "end": v(-80, 80) * mm});
            skCircle(sketch, "E79.5", {"center": v(-60, 67.5) * mm, "radius": 4 * mm});
            skCircle(sketch, "E79.6", {"center": v(60, 67.5) * mm, "radius": 4 * mm});
            skLineSegment(sketch, "E79.7", {"start": v(-70, -90) * mm, "end": v(70, -90) * mm});
            skArc(sketch, "E79.8", {"start": v(-80, -80) * mm, "mid": v(-77.07, -87.07) * mm, "end": v(-70, -90) * mm});
            skCircle(sketch, "E79.9", {"center": v(-60, -67.5) * mm, "radius": 4 * mm});
            skArc(sketch, "E79.10", {"start": v(70, -90) * mm, "mid": v(77.07, -87.07) * mm, "end": v(80, -80) * mm});
            skCircle(sketch, "E79.11", {"center": v(60, -67.5) * mm, "radius": 4 * mm});
            skArc(sketch, "E79.12", {"start": v(-56.15, -48.18) * mm, "mid": v(0, -67.5) * mm, "end": v(56.15, -48.18) * mm});
            skArc(sketch, "E79.13", {"start": v(56.15, -48.18) * mm, "mid": v(58.99, -44.68) * mm, "end": v(60, -40.3) * mm});
            skLineSegment(sketch, "E79.14", {"start": v(60, 40.3) * mm, "end": v(60, -40.3) * mm});
            skArc(sketch, "E79.15", {"start": v(60, 40.3) * mm, "mid": v(58.99, 44.68) * mm, "end": v(56.15, 48.18) * mm});
            skArc(sketch, "E79.16", {"start": v(56.15, 48.18) * mm, "mid": v(0, 67.5) * mm, "end": v(-56.15, 48.18) * mm});
            skArc(sketch, "E79.17", {"start": v(-56.15, 48.18) * mm, "mid": v(-58.99, 44.68) * mm, "end": v(-60, 40.3) * mm});
            skLineSegment(sketch, "E79.18", {"start": v(-60, 40.3) * mm, "end": v(-60, -40.3) * mm});
            skArc(sketch, "E79.19", {"start": v(-60, -40.3) * mm, "mid": v(-58.99, -44.68) * mm, "end": v(-56.15, -48.18) * mm});
            skLineSegment(sketch, "E80", {"start": v(0, 90) * mm, "end": v(0, 120) * mm, "construction": true});
            skPoint(sketch, "E80.endSnap0", {"position": v(0, 90) * mm});
            skCircle(sketch, "E81", {"center": v(0, 120) * mm, "radius": 6 * mm});
            skArc(sketch, "E82", {"start": v(-15, 120) * mm, "mid": v(0, 135) * mm, "end": v(15, 120) * mm});
            skLineSegment(sketch, "E83", {"start": v(-15, 120) * mm, "end": v(-15, 108) * mm});
            skLineSegment(sketch, "E84", {"start": v(-15, 108) * mm, "end": v(-33, 90) * mm});
            skLineSegment(sketch, "E85", {"start": v(15, 120) * mm, "end": v(15, 108) * mm});
            skLineSegment(sketch, "E86", {"start": v(15, 108) * mm, "end": v(33, 90) * mm});
            skLineSegment(sketch, "E87", {"start": v(-80, 0) * mm, "end": v(80, 0) * mm, "construction": true});
            skArc(sketch, "E88.MirrorCS", {"start": v(15, 120) * mm, "mid": v(0, 135) * mm, "end": v(-15, 120) * mm});
            skLineSegment(sketch, "E89.MirrorCS", {"start": v(-15, -108) * mm, "end": v(-33, -90) * mm});
            skLineSegment(sketch, "E90.MirrorCS", {"start": v(-15, -120) * mm, "end": v(-15, -108) * mm});
            skArc(sketch, "E91.MirrorCS", {"start": v(-15, -120) * mm, "mid": v(0, -135) * mm, "end": v(15, -120) * mm});
            skCircle(sketch, "E92.MirrorC", {"center": v(0, -120) * mm, "radius": 6 * mm});
            skLineSegment(sketch, "E93.MirrorCS", {"start": v(15, -120) * mm, "end": v(15, -108) * mm});
            skLineSegment(sketch, "E94.MirrorCS", {"start": v(15, -108) * mm, "end": v(33, -90) * mm});
            skLineSegment(sketch, "E95.MirrorCS", {"start": v(0, -90) * mm, "end": v(0, -120) * mm, "construction": true});
            skSolve(sketch);
        }
        {
            var Q0;
            Q0 = qSketchRegion(id + "F16", true);
            var Q1;
            Q1=makeQuery(id+"F2.opExtrude","CAP_FACE",FACE,{"disambiguationData":[OSD([sQuery(id+"F0.wireOp",EDGE,"E12"),sQuery(id+"F0.wireOp",EDGE,"E13"),sQuery(id+"F0.wireOp",EDGE,"E14"),sQuery(id+"F0.wireOp",EDGE,"E15"),sQuery(id+"F0.wireOp",EDGE,"E17.filletArc"),sQuery(id+"F0.wireOp",EDGE,"E18.filletArc"),sQuery(id+"F0.wireOp",EDGE,"E19.filletArc"),sQuery(id+"F0.wireOp",EDGE,"E20.filletArc"),sQuery(id+"F0.wireOp",EDGE,"E25.0"),sQuery(id+"F0.wireOp",EDGE,"E25.1"),sQuery(id+"F0.wireOp",EDGE,"E25.2"),sQuery(id+"F0.wireOp",EDGE,"E25.3"),sQuery(id+"F0.wireOp",EDGE,"E25.4"),sQuery(id+"F0.wireOp",EDGE,"E25.5"),sQuery(id+"F0.wireOp",EDGE,"E25.6"),sQuery(id+"F0.wireOp",EDGE,"E25.7")])],"isStart":false});
            extrude(context, id + "F17", {"entities" : qUnion([Q0]), "endBound" : BoundingType.UP_TO_SURFACE, "endBoundEntityFace" : qUnion([Q1]), "depth" : 25 * mm});
        }
    });
